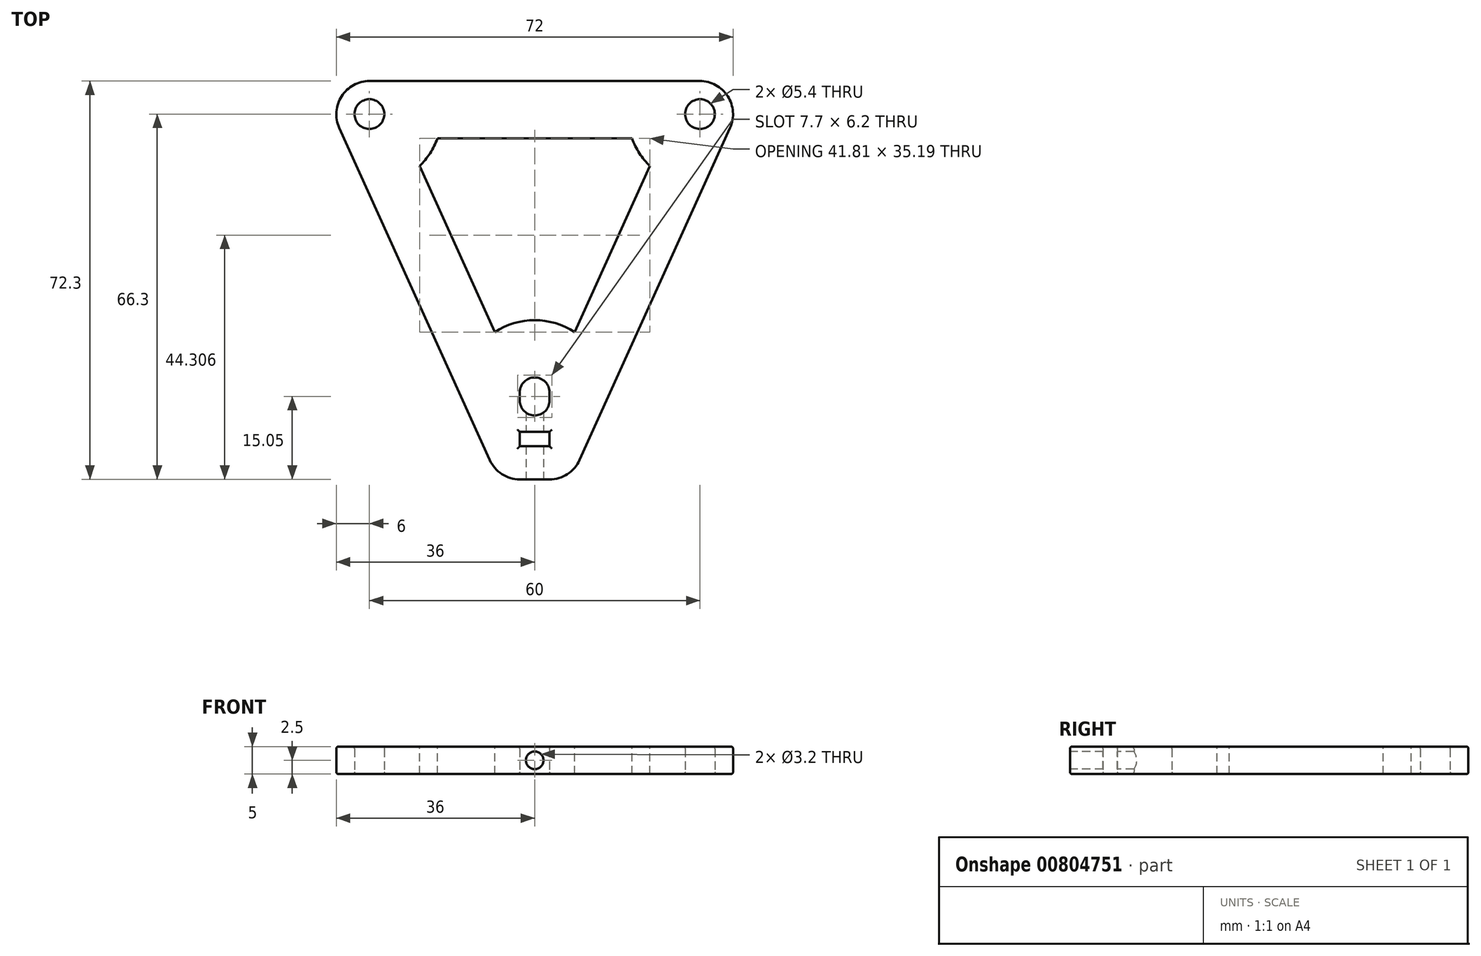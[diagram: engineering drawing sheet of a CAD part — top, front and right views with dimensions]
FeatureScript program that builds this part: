
annotation { "Feature Type Name" : "Feature", "Feature Type Description" : "" }
export const myFeature = defineFeature(function(context is Context, id is Id, definition is map)
    precondition{}
    {
        {
            var Q0;
            Q0=qCreatedBy(makeId("Top.planeOp"),FACE);
            var sketch = newSketch(context, id + "F0", { "sketchPlane" : qUnion([Q0])});
            skLineSegment(sketch, "E0", {"start": v(0, 26.9) * mm, "end": v(-30, 26.9) * mm});
            skLineSegment(sketch, "E1", {"start": v(0, -45.4) * mm, "end": v(0, -39.4) * mm});
            skLineSegment(sketch, "E2", {"start": v(0, -45.4) * mm, "end": v(-2.7, -45.4) * mm});
            skLineSegment(sketch, "E3", {"start": v(-8.17, -41.87) * mm, "end": v(-35.47, 18.43) * mm});
            skCircle(sketch, "E4", {"center": v(-30, 20.9) * mm, "radius": 2.7 * mm});
            skArc(sketch, "E5.0.startCap", {"start": v(0, -33.8) * mm, "mid": v(-1.9, -33) * mm, "end": v(-2.7, -31.1) * mm});
            skArc(sketch, "E5.0.endCap", {"start": v(-2.7, -29.6) * mm, "mid": v(-1.9, -27.7) * mm, "end": v(0, -26.9) * mm});
            skLineSegment(sketch, "E5.0.left", {"start": v(-2.7, -31.1) * mm, "end": v(-2.7, -29.6) * mm});
            skPoint(sketch, "E6.visualSharp", {"position": v(-39.3, 26.9) * mm});
            skArc(sketch, "E6.filletArc", {"start": v(-30, 26.9) * mm, "mid": v(-35.04, 24.15) * mm, "end": v(-35.47, 18.43) * mm});
            skPoint(sketch, "E7.visualSharp", {"position": v(-6.57, -45.4) * mm});
            skArc(sketch, "E7.filletArc", {"start": v(-8.17, -41.87) * mm, "mid": v(-5.95, -44.44) * mm, "end": v(-2.7, -45.4) * mm});
            skLineSegment(sketch, "E8.trimOffspring", {"start": v(0, -26.9) * mm, "end": v(0, 26.9) * mm});
            skLineSegment(sketch, "E9.bottom", {"start": v(0, -36.8) * mm, "end": v(-2.7, -36.8) * mm});
            skLineSegment(sketch, "E9.top", {"start": v(0, -39.4) * mm, "end": v(-2.7, -39.4) * mm});
            skLineSegment(sketch, "E9.right", {"start": v(-2.7, -36.8) * mm, "end": v(-2.7, -39.4) * mm});
            skLineSegment(sketch, "E10.trimOffspring", {"start": v(0, -36.8) * mm, "end": v(0, -33.8) * mm});
            skSolve(sketch);
        }
        {
            var Q0;
            Q0=makeQuery(id+"F0.imprint","IMPRINT",FACE,{"disambiguationData":[TD([[makeQuery(id+"F0.imprint","IMPRINT",EDGE,{"derivedFrom":sQuery(id+"F0.wireOp",EDGE,"E0")}),1.0]])]});
            extrude(context, id + "F1", {"entities" : qUnion([Q0]), "depth" : 5 * mm, "offsetDistance" : 25 * mm});
        }
        {
            var Q0;
            Q0=makeQuery(id+"F1.opExtrude","CAP_FACE",FACE,{"disambiguationData":[OSD([sQuery(id+"F0.wireOp",EDGE,"E0"),sQuery(id+"F0.wireOp",EDGE,"E1"),sQuery(id+"F0.wireOp",EDGE,"E2"),sQuery(id+"F0.wireOp",EDGE,"E3"),sQuery(id+"F0.wireOp",EDGE,"E4"),sQuery(id+"F0.wireOp",EDGE,"E5.0.startCap"),sQuery(id+"F0.wireOp",EDGE,"E5.0.endCap"),sQuery(id+"F0.wireOp",EDGE,"E5.0.left"),sQuery(id+"F0.wireOp",EDGE,"E6.filletArc"),sQuery(id+"F0.wireOp",EDGE,"E7.filletArc"),sQuery(id+"F0.wireOp",EDGE,"E8.trimOffspring"),sQuery(id+"F0.wireOp",EDGE,"E9.bottom"),sQuery(id+"F0.wireOp",EDGE,"E9.top"),sQuery(id+"F0.wireOp",EDGE,"E9.right"),sQuery(id+"F0.wireOp",EDGE,"E10.trimOffspring")])],"isStart":false});
            var sketch = newSketch(context, id + "F2", { "sketchPlane" : qUnion([Q0])});
            skLineSegment(sketch, "E11", {"start": v(0, 16.5) * mm, "end": v(-17.66, 16.5) * mm});
            skLineSegment(sketch, "E12", {"start": v(-20.9, 11.47) * mm, "end": v(-7.25, -18.69) * mm});
            skArc(sketch, "E13", {"start": v(0, -16.5) * mm, "mid": v(-3.79, -17.06) * mm, "end": v(-7.25, -18.69) * mm});
            skArc(sketch, "E14", {"start": v(-20.9, 11.47) * mm, "mid": v(-19, 13.8) * mm, "end": v(-17.66, 16.5) * mm});
            skLineSegment(sketch, "E15.trimOffspring", {"start": v(0, -16.5) * mm, "end": v(0, 16.5) * mm});
            skSolve(sketch);
        }
        {
            var Q0;
            Q0=qSketchRegion(id+"F2",true);
            extrude(context, id + "F3", {"entities" : qUnion([Q0]), "operationType" : NewBodyOperationType.REMOVE, "endBound" : BoundingType.UP_TO_NEXT, "oppositeDirection" : true, "depth" : 25 * mm, "offsetDistance" : 25 * mm});
        }
        {
            var Q0;
            Q0=makeQuery(id+"F1.opExtrude","SWEPT_FACE",FACE,{"disambiguationData":[OSD([sQuery(id+"F0.wireOp",EDGE,"E2")])]});
            var sketch = newSketch(context, id + "F4", { "sketchPlane" : qUnion([Q0])});
            skCircle(sketch, "E16", {"center": v(0, 2.5) * mm, "radius": 1.6 * mm});
            skSolve(sketch);
        }
        {
            var Q0;
            Q0=qSketchRegion(id+"F4",true);
            var Q1;
            Q1=makeQuery(id+"F1.opExtrude","SWEPT_FACE",FACE,{"disambiguationData":[OSD([sQuery(id+"F0.wireOp",EDGE,"E5.0.startCap")])]});
            extrude(context, id + "F5", {"entities" : qUnion([Q0]), "operationType" : NewBodyOperationType.REMOVE, "endBound" : BoundingType.UP_TO_SURFACE, "oppositeDirection" : true, "depth" : 25 * mm, "endBoundEntityFace" : qUnion([Q1]), "offsetDistance" : 25 * mm});
        }
        {
            var Q0;
            Q0=makeQuery(id+"F1.opExtrude","CAP_EDGE",EDGE,{"disambiguationData":[OSD([sQuery(id+"F0.wireOp",EDGE,"E3")])],"isStart":false});
            var Q1;
            Q1=makeQuery(id+"F1.opExtrude","CAP_EDGE",EDGE,{"disambiguationData":[OSD([sQuery(id+"F0.wireOp",EDGE,"E7.filletArc")])],"isStart":true});
            var Q2;
            Q2=makeQuery(id+"F5.boolean.opBoolean","COPY",EDGE,{"derivedFrom":makeQuery(id+"F5.opExtrude","CAP_EDGE",EDGE,{"disambiguationData":[OSD([sQuery(id+"F4.wireOp",EDGE,"E16")])],"isStart":true})});
            var Q3;
            Q3=makeQuery(id+"F1.opExtrude","CAP_EDGE",EDGE,{"disambiguationData":[OSD([sQuery(id+"F0.wireOp",EDGE,"E9.right")])],"isStart":false});
            var Q4;
            Q4=makeQuery(id+"F1.opExtrude","CAP_EDGE",EDGE,{"disambiguationData":[OSD([sQuery(id+"F0.wireOp",EDGE,"E9.top")])],"isStart":false});
            var Q5;
            Q5=makeQuery(id+"F1.opExtrude","CAP_EDGE",EDGE,{"disambiguationData":[OSD([sQuery(id+"F0.wireOp",EDGE,"E9.bottom")])],"isStart":false});
            var Q6;
            Q6=makeQuery(id+"F1.opExtrude","CAP_EDGE",EDGE,{"disambiguationData":[OSD([sQuery(id+"F0.wireOp",EDGE,"E9.top")])],"isStart":true});
            var Q7;
            Q7=makeQuery(id+"F1.opExtrude","CAP_EDGE",EDGE,{"disambiguationData":[OSD([sQuery(id+"F0.wireOp",EDGE,"E9.right")])],"isStart":true});
            var Q8;
            Q8=makeQuery(id+"F1.opExtrude","CAP_EDGE",EDGE,{"disambiguationData":[OSD([sQuery(id+"F0.wireOp",EDGE,"E9.bottom")])],"isStart":true});
            var Q9;
            Q9=makeQuery(id+"F1.opExtrude","CAP_EDGE",EDGE,{"disambiguationData":[OSD([sQuery(id+"F0.wireOp",EDGE,"E4")])],"isStart":false});
            var Q10;
            Q10=makeQuery(id+"F1.opExtrude","CAP_EDGE",EDGE,{"disambiguationData":[OSD([sQuery(id+"F0.wireOp",EDGE,"E4")])],"isStart":true});
            var Q11;
            Q11=makeQuery(id+"F1.opExtrude","CAP_EDGE",EDGE,{"disambiguationData":[OSD([sQuery(id+"F0.wireOp",EDGE,"E5.0.startCap")])],"isStart":true});
            var Q12;
            Q12=makeQuery(id+"F1.opExtrude","CAP_EDGE",EDGE,{"disambiguationData":[OSD([sQuery(id+"F0.wireOp",EDGE,"E5.0.left")])],"isStart":false});
            fillet(context, id + "F6", {"entities" : qUnion([Q0, Q1, Q2, Q3, Q4, Q5, Q6, Q7, Q8, Q9, Q10, Q11, Q12]), "radius" : 0.4 * mm, "tangentPropagation" : true, "allowEdgeOverflow" : false});
        }
        {
            var Q0;
            Q0=makeQuery(id+"F1.opExtrude","SWEPT_BODY",BODY,{"disambiguationData":[OSD([sQuery(id+"F0.wireOp",EDGE,"E0"),sQuery(id+"F0.wireOp",EDGE,"E1"),sQuery(id+"F0.wireOp",EDGE,"E2"),sQuery(id+"F0.wireOp",EDGE,"E3"),sQuery(id+"F0.wireOp",EDGE,"E4"),sQuery(id+"F0.wireOp",EDGE,"E5.0.startCap"),sQuery(id+"F0.wireOp",EDGE,"E5.0.endCap"),sQuery(id+"F0.wireOp",EDGE,"E5.0.left"),sQuery(id+"F0.wireOp",EDGE,"E6.filletArc"),sQuery(id+"F0.wireOp",EDGE,"E7.filletArc"),sQuery(id+"F0.wireOp",EDGE,"E8.trimOffspring"),sQuery(id+"F0.wireOp",EDGE,"E9.bottom"),sQuery(id+"F0.wireOp",EDGE,"E9.top"),sQuery(id+"F0.wireOp",EDGE,"E9.right"),sQuery(id+"F0.wireOp",EDGE,"E10.trimOffspring")])]});
            var Q1;
            {var subQ0=sQuery(id+"F0.wireOp",EDGE,"E0");var subQ5=sQuery(id+"F0.wireOp",EDGE,"E8.trimOffspring");Q1=makeQuery(id+"F3.boolean.opBoolean","SPLIT",FACE,{"disambiguationData":[TD([makeQuery(id+"F1.opExtrude","SWEPT_FACE",FACE,{"disambiguationData":[OSD([subQ0])]})])],"derivedFrom":makeQuery(id+"F1.opExtrude","SWEPT_FACE",FACE,{"disambiguationData":[OSD([subQ5])]})});}
            mirror(context, id + "F7", {"operationType" : NewBodyOperationType.ADD, "entities" : qUnion([Q0]), "mirrorPlane" : qUnion([Q1])});
        }
    });
